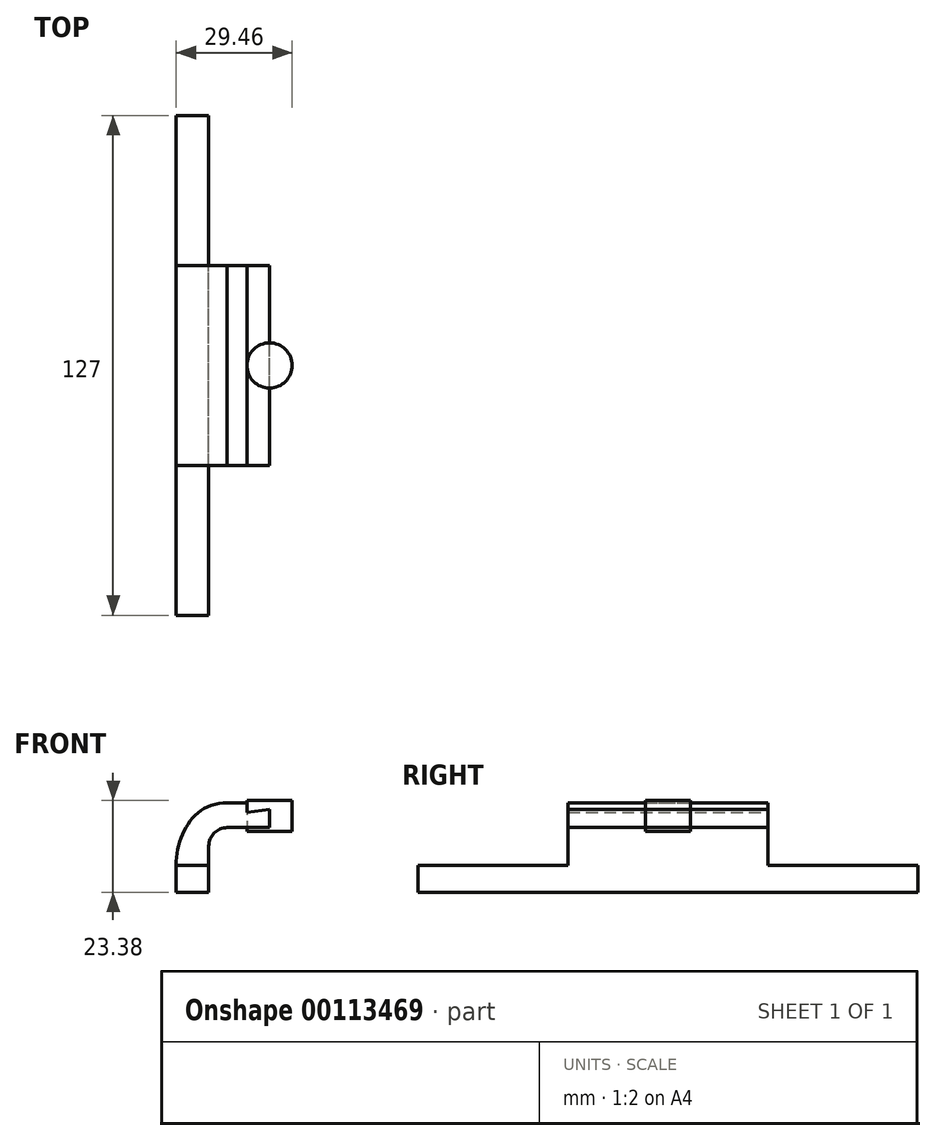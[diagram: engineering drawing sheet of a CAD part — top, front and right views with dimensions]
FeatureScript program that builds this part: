
annotation { "Feature Type Name" : "Feature", "Feature Type Description" : "" }
export const myFeature = defineFeature(function(context is Context, id is Id, definition is map)
    precondition{}
    {
        {
            var Q0;
            Q0=qCreatedBy(makeId("Front.planeOp"),FACE);
            var sketch = newSketch(context, id + "F0", { "sketchPlane" : qUnion([Q0])});
            skLineSegment(sketch, "E0.bottom", {"start": v(-4.14, -3.44) * mm, "end": v(4.14, -3.44) * mm});
            skLineSegment(sketch, "E0.top", {"start": v(-4.14, 3.44) * mm, "end": v(4.14, 3.44) * mm});
            skLineSegment(sketch, "E0.left", {"start": v(-4.14, -3.44) * mm, "end": v(-4.14, 3.44) * mm});
            skLineSegment(sketch, "E0.right", {"start": v(4.14, -3.44) * mm, "end": v(4.14, 3.44) * mm});
            skPoint(sketch, "E0.middle", {"position": v(0, 0) * mm});
            skLineSegment(sketch, "E1.bottom", {"start": v(25.32, 12.1) * mm, "end": v(13.83, 12.1) * mm});
            skLineSegment(sketch, "E1.top", {"start": v(25.32, 19.94) * mm, "end": v(13.83, 19.94) * mm});
            skLineSegment(sketch, "E1.left", {"start": v(25.32, 12.1) * mm, "end": v(25.32, 19.94) * mm});
            skLineSegment(sketch, "E1.right", {"start": v(13.83, 12.1) * mm, "end": v(13.83, 19.94) * mm});
            skPoint(sketch, "E1.middle", {"position": v(19.57, 16.02) * mm});
            skLineSegment(sketch, "E2", {"start": v(4.14, 3.44) * mm, "end": v(4.14, 8.32) * mm});
            skArc(sketch, "E3", {"start": v(4.14, 8.32) * mm, "mid": v(5.51, 11.64) * mm, "end": v(8.83, 13.02) * mm});
            skLineSegment(sketch, "E4", {"start": v(8.83, 13.02) * mm, "end": v(19.57, 13.02) * mm});
            skLineSegment(sketch, "E5", {"start": v(19.57, 16.02) * mm, "end": v(19.57, 13.02) * mm});
            skLineSegment(sketch, "E6", {"start": v(19.57, 16.02) * mm, "end": v(19.57, 16.02) * mm});
            skPoint(sketch, "E6.endSnap0", {"position": v(19.57, 19.94) * mm});
            skLineSegment(sketch, "E7", {"start": v(19.57, 19.27) * mm, "end": v(8.83, 19.27) * mm});
            skLineSegment(sketch, "E8", {"start": v(19.57, 16.02) * mm, "end": v(19.57, 19.27) * mm});
            skFitSpline(sketch, "E9", {"points": [v(8.83, 19.27) * mm, v(-4.14, 3.44) * mm], "startDerivative": vector(-25.8, 0.8) * mm, "endDerivative": vector(0.09, -22.72) * mm});
            skLineSegment(sketch, "E10", {"start": v(19.57, 19.94) * mm, "end": v(19.57, 12.1) * mm});
            skArc(sketch, "E11.0", {"start": v(0.96, 8.32) * mm, "mid": v(3.42, 14.04) * mm, "end": v(9.26, 16.18) * mm});
            skLineSegment(sketch, "E11.1", {"start": v(0.96, 3.45) * mm, "end": v(0.96, 8.32) * mm});
            skLineSegment(sketch, "E12", {"start": v(9.26, 16.18) * mm, "end": v(19.57, 17.64) * mm});
            skSolve(sketch);
        }
        {
            var Q0;
            Q0=makeQuery(id+"F0.imprint","IMPRINT",FACE,{"disambiguationData":[TD([[makeQuery(id+"F0.imprint","IMPRINT",EDGE,{"derivedFrom":sQuery(id+"F0.wireOp",EDGE,"E0.bottom")}),1.0]])]});
            extrude(context, id + "F1", {"entities" : qUnion([Q0]), "endBound" : BoundingType.SYMMETRIC, "depth" : 127 * mm});
        }
        {
            var Q0;
            Q0=makeQuery(id+"F0.imprint","IMPRINT",FACE,{"disambiguationData":[TD([[makeQuery(id+"F0.imprint","IMPRINT",EDGE,{"derivedFrom":sQuery(id+"F0.wireOp",EDGE,"E0.top")}),1.0]])]});
            var Q1;
            {var subQ0=sQuery(id+"F0.wireOp",EDGE,"E5");Q1=makeQuery(id+"F0.imprint","IMPRINT",FACE,{"disambiguationData":[TD([[makeQuery(id+"F0.imprint","IMPRINT",EDGE,{"derivedFrom":subQ0}),-1.0]])]});}
            extrude(context, id + "F2", {"entities" : qUnion([Q0, Q1]), "operationType" : NewBodyOperationType.ADD, "endBound" : BoundingType.SYMMETRIC, "depth" : 50.8 * mm});
        }
        {
            var Q0;
            {var subQ0=sQuery(id+"F0.wireOp",EDGE,"E1.left");Q0=makeQuery(id+"F0.imprint","IMPRINT",FACE,{"disambiguationData":[TD([[makeQuery(id+"F0.imprint","IMPRINT",EDGE,{"derivedFrom":subQ0}),1.0]])]});}
            var Q1;
            Q1=sQuery(id+"F0.wireOp",EDGE,"E8");
            revolve(context, id + "F3", {"entities" : qUnion([Q0]), "axis" : qUnion([Q1]), "revolveType" : RevolveType.FULL});
        }
    });
